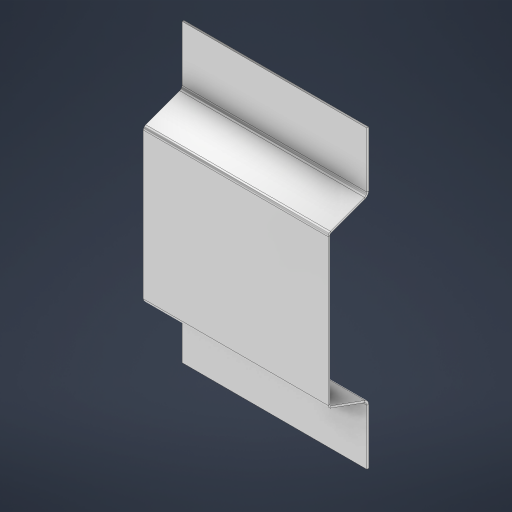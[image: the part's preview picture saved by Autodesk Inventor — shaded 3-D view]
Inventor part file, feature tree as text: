
AUTODESK INVENTOR PART (.ipt)
format: ipt  version: 2024.3 (Build 283343010, 343A)  size: 211,456 bytes
history: native  units: mm
features: other x4, sketch x2
ambient origin geometry x8: Origin, YZ Plane, XZ Plane, XY Plane, X Axis, Y Axis, Z Axis, Center Point
bodies: Volumenkörper1 (feature_tree)
feature tree (6):
  sketch  "Skizze1"  dims[d0=0.1mm]
  other  "Konturlasche1"
  sketch  "Skizze2"  dims[d1=10.0mm d2=2.1mm d3=10.0mm d4=3.0mm d5=0.2mm d6=0.1mm d7=0.1mm d8=0.05mm d9=0.2mm d10=0.1mm d11=10.0mm d12=0.1mm d13=0.5mm d14=0.4mm d15=0.1mm d16=0.1mm d17=12.217305mm]
  other  "Grobblech1"
  other  "Biegung1"
  other  "Ecke1"
